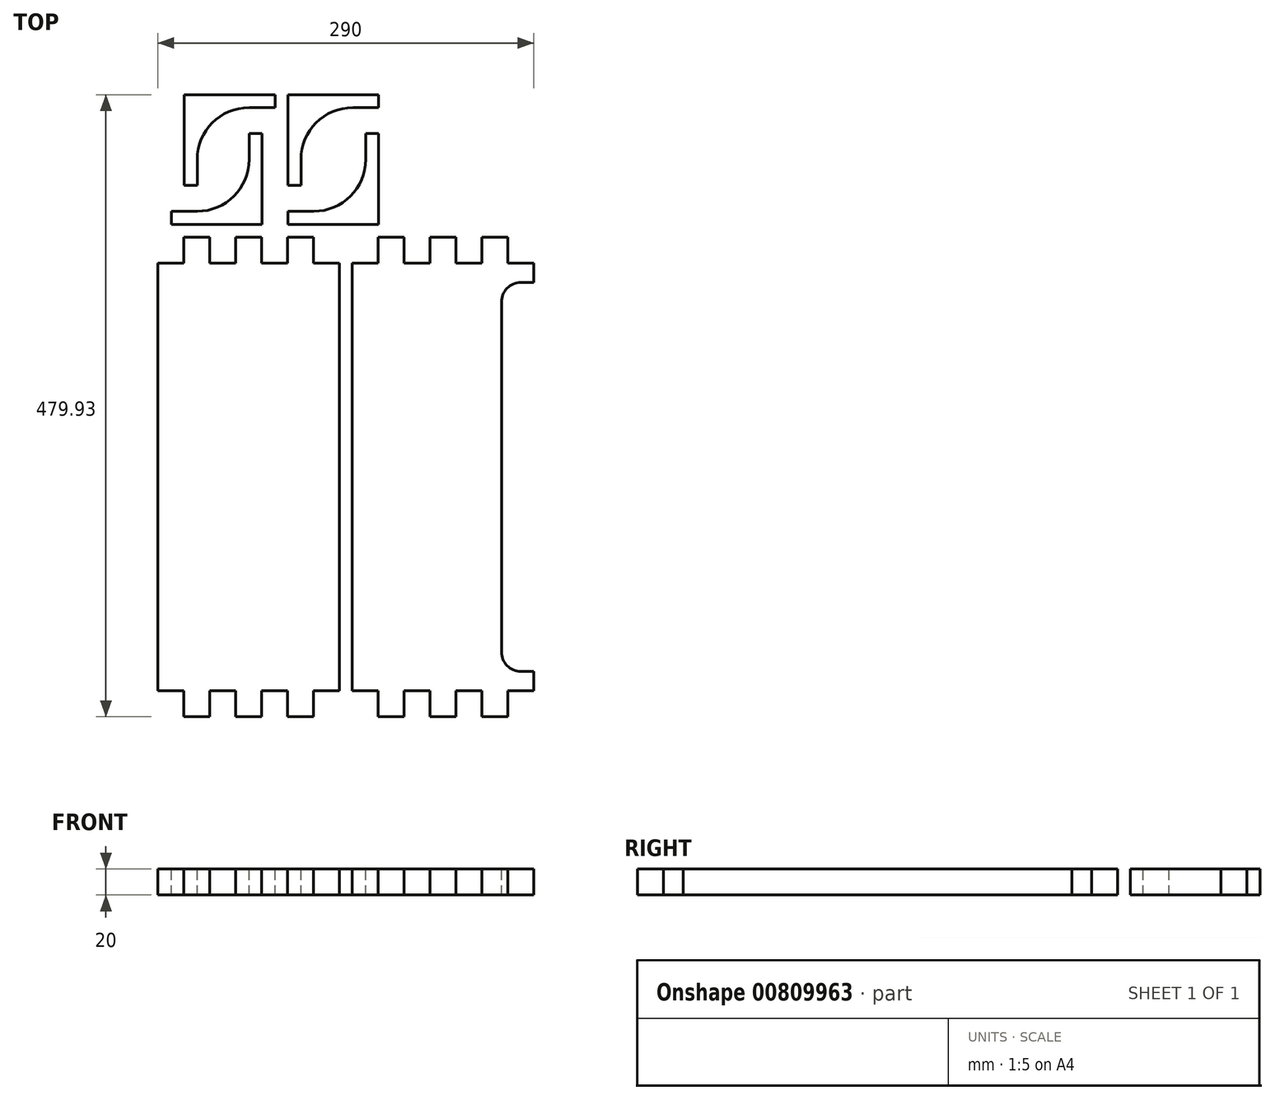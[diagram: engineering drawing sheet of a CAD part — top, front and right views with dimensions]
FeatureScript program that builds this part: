
annotation { "Feature Type Name" : "Feature", "Feature Type Description" : "" }
export const myFeature = defineFeature(function(context is Context, id is Id, definition is map)
    precondition{}
    {
        {
            var Q0;
            Q0=qCreatedBy(makeId("Top.planeOp"),FACE);
            var sketch = newSketch(context, id + "F0", { "sketchPlane" : qUnion([Q0])});
            skLineSegment(sketch, "E0", {"start": v(-70, 25) * mm, "end": v(-50, 25) * mm});
            skLineSegment(sketch, "E1", {"start": v(-50, 25) * mm, "end": v(-50, 5) * mm});
            skLineSegment(sketch, "E2", {"start": v(-50, 5) * mm, "end": v(-30, 5) * mm});
            skLineSegment(sketch, "E3", {"start": v(-30, 5) * mm, "end": v(-30, 25) * mm});
            skLineSegment(sketch, "E4", {"start": v(-30, 25) * mm, "end": v(-10, 25) * mm});
            skLineSegment(sketch, "E5", {"start": v(-10, 25) * mm, "end": v(-10, 5) * mm});
            skLineSegment(sketch, "E6", {"start": v(-10, 5) * mm, "end": v(10, 5) * mm});
            skLineSegment(sketch, "E7", {"start": v(10, 5) * mm, "end": v(10, 25) * mm});
            skLineSegment(sketch, "E8", {"start": v(10, 25) * mm, "end": v(30, 25) * mm});
            skLineSegment(sketch, "E9", {"start": v(30, 25) * mm, "end": v(30, 5) * mm});
            skLineSegment(sketch, "E10", {"start": v(30, 5) * mm, "end": v(50, 5) * mm});
            skLineSegment(sketch, "E11", {"start": v(50, 5) * mm, "end": v(50, 25) * mm});
            skLineSegment(sketch, "E12", {"start": v(50, 25) * mm, "end": v(70, 25) * mm});
            skLineSegment(sketch, "E13", {"start": v(-70, 25) * mm, "end": v(-70, 190) * mm});
            skLineSegment(sketch, "E14", {"start": v(70, 190) * mm, "end": v(70, 25) * mm});
            skLineSegment(sketch, "E15.MirrorCS", {"start": v(-10, 355) * mm, "end": v(-10, 375) * mm});
            skLineSegment(sketch, "E16.MirrorCS", {"start": v(-50, 355) * mm, "end": v(-50, 375) * mm});
            skLineSegment(sketch, "E17.MirrorCS", {"start": v(10, 375) * mm, "end": v(10, 355) * mm});
            skLineSegment(sketch, "E18.MirrorCS", {"start": v(-30, 355) * mm, "end": v(-10, 355) * mm});
            skLineSegment(sketch, "E19.MirrorCS", {"start": v(50, 355) * mm, "end": v(70, 355) * mm});
            skLineSegment(sketch, "E20.MirrorCS", {"start": v(-50, 375) * mm, "end": v(-30, 375) * mm});
            skLineSegment(sketch, "E21.MirrorCS", {"start": v(30, 375) * mm, "end": v(50, 375) * mm});
            skLineSegment(sketch, "E22.MirrorCS", {"start": v(30, 355) * mm, "end": v(30, 375) * mm});
            skLineSegment(sketch, "E23.MirrorCS", {"start": v(10, 355) * mm, "end": v(30, 355) * mm});
            skLineSegment(sketch, "E24.MirrorCS", {"start": v(-70, 355) * mm, "end": v(-50, 355) * mm});
            skLineSegment(sketch, "E25.MirrorCS", {"start": v(70, 190) * mm, "end": v(70, 355) * mm});
            skLineSegment(sketch, "E26.MirrorCS", {"start": v(-10, 375) * mm, "end": v(10, 375) * mm});
            skLineSegment(sketch, "E27.MirrorCS", {"start": v(-70, 355) * mm, "end": v(-70, 190) * mm});
            skLineSegment(sketch, "E28.MirrorCS", {"start": v(50, 375) * mm, "end": v(50, 355) * mm});
            skLineSegment(sketch, "E29.MirrorCS", {"start": v(-30, 375) * mm, "end": v(-30, 355) * mm});
            skLineSegment(sketch, "E30.MirrorCS", {"start": v(220, 25) * mm, "end": v(200, 25) * mm});
            skLineSegment(sketch, "E31.MirrorCS", {"start": v(180, 375) * mm, "end": v(180, 355) * mm});
            skLineSegment(sketch, "E32.MirrorCS", {"start": v(100, 375) * mm, "end": v(100, 355) * mm});
            skLineSegment(sketch, "E33.MirrorCS", {"start": v(160, 375) * mm, "end": v(140, 375) * mm});
            skLineSegment(sketch, "E34.MirrorCS", {"start": v(100, 25) * mm, "end": v(80, 25) * mm});
            skLineSegment(sketch, "E35.MirrorCS", {"start": v(140, 375) * mm, "end": v(140, 355) * mm});
            skLineSegment(sketch, "E36.MirrorCS", {"start": v(180, 25) * mm, "end": v(160, 25) * mm});
            skLineSegment(sketch, "E37.MirrorCS", {"start": v(100, 5) * mm, "end": v(100, 25) * mm});
            skLineSegment(sketch, "E38.MirrorCS", {"start": v(200, 355) * mm, "end": v(200, 375) * mm});
            skLineSegment(sketch, "E39.MirrorCS", {"start": v(180, 5) * mm, "end": v(180, 25) * mm});
            skLineSegment(sketch, "E40.MirrorCS", {"start": v(120, 5) * mm, "end": v(100, 5) * mm});
            skLineSegment(sketch, "E41.MirrorCS", {"start": v(140, 355) * mm, "end": v(120, 355) * mm});
            skLineSegment(sketch, "E42.MirrorCS", {"start": v(160, 355) * mm, "end": v(160, 375) * mm});
            skLineSegment(sketch, "E43.MirrorCS", {"start": v(200, 5) * mm, "end": v(180, 5) * mm});
            skLineSegment(sketch, "E44.MirrorCS", {"start": v(120, 25) * mm, "end": v(120, 5) * mm});
            skLineSegment(sketch, "E45.MirrorCS", {"start": v(120, 355) * mm, "end": v(120, 375) * mm});
            skLineSegment(sketch, "E46.MirrorCS", {"start": v(200, 25) * mm, "end": v(200, 5) * mm});
            skLineSegment(sketch, "E47.MirrorCS", {"start": v(140, 25) * mm, "end": v(120, 25) * mm});
            skLineSegment(sketch, "E48.MirrorCS", {"start": v(120, 375) * mm, "end": v(100, 375) * mm});
            skLineSegment(sketch, "E49.MirrorCS", {"start": v(200, 375) * mm, "end": v(180, 375) * mm});
            skLineSegment(sketch, "E50.MirrorCS", {"start": v(140, 5) * mm, "end": v(140, 25) * mm});
            skLineSegment(sketch, "E51.MirrorCS", {"start": v(100, 355) * mm, "end": v(80, 355) * mm});
            skLineSegment(sketch, "E52.MirrorCS", {"start": v(160, 5) * mm, "end": v(140, 5) * mm});
            skLineSegment(sketch, "E53.MirrorCS", {"start": v(180, 355) * mm, "end": v(160, 355) * mm});
            skLineSegment(sketch, "E54.MirrorCS", {"start": v(160, 25) * mm, "end": v(160, 5) * mm});
            skLineSegment(sketch, "E55.MirrorCS", {"start": v(220, 355) * mm, "end": v(200, 355) * mm});
            skLineSegment(sketch, "E56", {"start": v(220, 355) * mm, "end": v(220, 340) * mm});
            skLineSegment(sketch, "E57", {"start": v(220, 25) * mm, "end": v(220, 40) * mm});
            skLineSegment(sketch, "E58", {"start": v(80, 355) * mm, "end": v(80, 25) * mm});
            skArc(sketch, "E59", {"start": v(220, 340) * mm, "mid": v(202.32, 332.68) * mm, "end": v(195, 315) * mm});
            skArc(sketch, "E60.MirrorCS", {"start": v(220, 40) * mm, "mid": v(202.32, 47.32) * mm, "end": v(195, 65) * mm});
            skLineSegment(sketch, "E61", {"start": v(195, 315) * mm, "end": v(195, 65) * mm});
            skLineSegment(sketch, "E62", {"start": v(-70, 385) * mm, "end": v(-70, 455) * mm});
            skLineSegment(sketch, "E63", {"start": v(-70, 455) * mm, "end": v(0, 455) * mm});
            skLineSegment(sketch, "E64", {"start": v(-70, 385) * mm, "end": v(-55, 385) * mm});
            skLineSegment(sketch, "E65", {"start": v(0, 455) * mm, "end": v(0, 440) * mm});
            skLineSegment(sketch, "E66", {"start": v(-55, 385) * mm, "end": v(-55, 400) * mm});
            skLineSegment(sketch, "E67", {"start": v(0, 440) * mm, "end": v(-15, 440) * mm});
            skArc(sketch, "E68", {"start": v(-15, 440) * mm, "mid": v(-43.28, 428.28) * mm, "end": v(-55, 400) * mm});
            skLineSegment(sketch, "E69", {"start": v(10, 455) * mm, "end": v(25, 455) * mm});
            skLineSegment(sketch, "E70", {"start": v(25, 455) * mm, "end": v(25, 385) * mm});
            skLineSegment(sketch, "E71", {"start": v(25, 385) * mm, "end": v(-45, 385) * mm});
            skLineSegment(sketch, "E72", {"start": v(-45, 385) * mm, "end": v(-45, 400) * mm});
            skLineSegment(sketch, "E73", {"start": v(-45, 400) * mm, "end": v(-30, 400) * mm});
            skLineSegment(sketch, "E74", {"start": v(10, 455) * mm, "end": v(10, 440) * mm});
            skArc(sketch, "E75", {"start": v(-30, 400) * mm, "mid": v(-1.72, 411.72) * mm, "end": v(10, 440) * mm});
            skLineSegment(sketch, "E76.MirrorCS", {"start": v(90, 455) * mm, "end": v(90, 440) * mm});
            skLineSegment(sketch, "E77.MirrorCS", {"start": v(145, 385) * mm, "end": v(145, 400) * mm});
            skLineSegment(sketch, "E78.MirrorCS", {"start": v(170, 385) * mm, "end": v(170, 455) * mm});
            skArc(sketch, "E79.MirrorCS", {"start": v(115, 440) * mm, "mid": v(143.28, 428.28) * mm, "end": v(155, 400) * mm});
            skLineSegment(sketch, "E80.MirrorCS", {"start": v(100, 440) * mm, "end": v(115, 440) * mm});
            skLineSegment(sketch, "E81.MirrorCS", {"start": v(155, 385) * mm, "end": v(155, 400) * mm});
            skLineSegment(sketch, "E82.MirrorCS", {"start": v(145, 400) * mm, "end": v(130, 400) * mm});
            skLineSegment(sketch, "E83.MirrorCS", {"start": v(170, 385) * mm, "end": v(155, 385) * mm});
            skLineSegment(sketch, "E84.MirrorCS", {"start": v(75, 385) * mm, "end": v(145, 385) * mm});
            skLineSegment(sketch, "E85.MirrorCS", {"start": v(75, 455) * mm, "end": v(75, 385) * mm});
            skLineSegment(sketch, "E86.MirrorCS", {"start": v(170, 455) * mm, "end": v(100, 455) * mm});
            skArc(sketch, "E87.MirrorCS", {"start": v(130, 400) * mm, "mid": v(101.72, 411.72) * mm, "end": v(90, 440) * mm});
            skLineSegment(sketch, "E88.MirrorCS", {"start": v(90, 455) * mm, "end": v(75, 455) * mm});
            skLineSegment(sketch, "E89.MirrorCS", {"start": v(100, 455) * mm, "end": v(100, 440) * mm});
            skLineSegment(sketch, "E90", {"start": v(220, -250) * mm, "end": v(220, -473) * mm});
            skLineSegment(sketch, "E91", {"start": v(80, -250) * mm, "end": v(80, -473) * mm});
            skLineSegment(sketch, "E92", {"start": v(220, -473) * mm, "end": v(220, -495) * mm});
            skLineSegment(sketch, "E93", {"start": v(80, -473) * mm, "end": v(80, -495) * mm});
            skLineSegment(sketch, "E94", {"start": v(80, -495) * mm, "end": v(99.5, -495) * mm});
            skLineSegment(sketch, "E95", {"start": v(99.5, -495) * mm, "end": v(99.5, -473) * mm});
            skLineSegment(sketch, "E96", {"start": v(99.5, -473) * mm, "end": v(120.5, -473) * mm});
            skLineSegment(sketch, "E97", {"start": v(120.5, -473) * mm, "end": v(120.5, -495) * mm});
            skLineSegment(sketch, "E98", {"start": v(120.5, -495) * mm, "end": v(139.5, -495) * mm});
            skLineSegment(sketch, "E99", {"start": v(139.5, -495) * mm, "end": v(139.5, -473) * mm});
            skLineSegment(sketch, "E100", {"start": v(139.5, -473) * mm, "end": v(160.5, -473) * mm});
            skLineSegment(sketch, "E101", {"start": v(160.5, -473) * mm, "end": v(160.5, -495) * mm});
            skLineSegment(sketch, "E102", {"start": v(160.5, -495) * mm, "end": v(179.5, -495) * mm});
            skLineSegment(sketch, "E103", {"start": v(179.5, -495) * mm, "end": v(179.5, -473) * mm});
            skLineSegment(sketch, "E104", {"start": v(179.5, -473) * mm, "end": v(200.5, -473) * mm});
            skLineSegment(sketch, "E105", {"start": v(200.5, -473) * mm, "end": v(200.5, -495) * mm});
            skLineSegment(sketch, "E106", {"start": v(200.5, -495) * mm, "end": v(220, -495) * mm});
            skLineSegment(sketch, "E107.MirrorCS", {"start": v(99.5, -27) * mm, "end": v(120.5, -27) * mm});
            skLineSegment(sketch, "E108.MirrorCS", {"start": v(200.5, -5) * mm, "end": v(220, -5) * mm});
            skLineSegment(sketch, "E109.MirrorCS", {"start": v(120.5, -5) * mm, "end": v(139.5, -5) * mm});
            skLineSegment(sketch, "E110.MirrorCS", {"start": v(139.5, -27) * mm, "end": v(160.5, -27) * mm});
            skLineSegment(sketch, "E111.MirrorCS", {"start": v(179.5, -5) * mm, "end": v(179.5, -27) * mm});
            skLineSegment(sketch, "E112.MirrorCS", {"start": v(220, -27) * mm, "end": v(220, -5) * mm});
            skLineSegment(sketch, "E113.MirrorCS", {"start": v(120.5, -27) * mm, "end": v(120.5, -5) * mm});
            skLineSegment(sketch, "E114.MirrorCS", {"start": v(80, -5) * mm, "end": v(99.5, -5) * mm});
            skLineSegment(sketch, "E115.MirrorCS", {"start": v(179.5, -27) * mm, "end": v(200.5, -27) * mm});
            skLineSegment(sketch, "E116.MirrorCS", {"start": v(139.5, -5) * mm, "end": v(139.5, -27) * mm});
            skLineSegment(sketch, "E117.MirrorCS", {"start": v(200.5, -27) * mm, "end": v(200.5, -5) * mm});
            skLineSegment(sketch, "E118.MirrorCS", {"start": v(99.5, -5) * mm, "end": v(99.5, -27) * mm});
            skLineSegment(sketch, "E119.MirrorCS", {"start": v(160.5, -5) * mm, "end": v(179.5, -5) * mm});
            skLineSegment(sketch, "E120.MirrorCS", {"start": v(160.5, -27) * mm, "end": v(160.5, -5) * mm});
            skLineSegment(sketch, "E121.MirrorCS", {"start": v(80, -27) * mm, "end": v(80, -5) * mm});
            skLineSegment(sketch, "E122.MirrorCS", {"start": v(80, -250) * mm, "end": v(80, -27) * mm});
            skLineSegment(sketch, "E123.MirrorCS", {"start": v(220, -250) * mm, "end": v(220, -27) * mm});
            skLineSegment(sketch, "E124.MirrorCS", {"start": v(29.5, -5) * mm, "end": v(10.5, -5) * mm});
            skLineSegment(sketch, "E125.MirrorCS", {"start": v(-70, -27) * mm, "end": v(-70, -5) * mm});
            skLineSegment(sketch, "E126.MirrorCS", {"start": v(10.5, -27) * mm, "end": v(-10.5, -27) * mm});
            skLineSegment(sketch, "E127.MirrorCS", {"start": v(10.5, -5) * mm, "end": v(10.5, -27) * mm});
            skLineSegment(sketch, "E128.MirrorCS", {"start": v(-50.5, -473) * mm, "end": v(-50.5, -495) * mm});
            skLineSegment(sketch, "E129.MirrorCS", {"start": v(-50.5, -495) * mm, "end": v(-70, -495) * mm});
            skLineSegment(sketch, "E130.MirrorCS", {"start": v(-29.5, -473) * mm, "end": v(-50.5, -473) * mm});
            skLineSegment(sketch, "E131.MirrorCS", {"start": v(50.5, -5) * mm, "end": v(50.5, -27) * mm});
            skLineSegment(sketch, "E132.MirrorCS", {"start": v(50.5, -495) * mm, "end": v(50.5, -473) * mm});
            skLineSegment(sketch, "E133.MirrorCS", {"start": v(-70, -473) * mm, "end": v(-70, -495) * mm});
            skLineSegment(sketch, "E134.MirrorCS", {"start": v(-10.5, -27) * mm, "end": v(-10.5, -5) * mm});
            skLineSegment(sketch, "E135.MirrorCS", {"start": v(-29.5, -495) * mm, "end": v(-29.5, -473) * mm});
            skLineSegment(sketch, "E136.MirrorCS", {"start": v(-10.5, -5) * mm, "end": v(-29.5, -5) * mm});
            skLineSegment(sketch, "E137.MirrorCS", {"start": v(29.5, -27) * mm, "end": v(29.5, -5) * mm});
            skLineSegment(sketch, "E138.MirrorCS", {"start": v(-29.5, -27) * mm, "end": v(-50.5, -27) * mm});
            skLineSegment(sketch, "E139.MirrorCS", {"start": v(-50.5, -5) * mm, "end": v(-70, -5) * mm});
            skLineSegment(sketch, "E140.MirrorCS", {"start": v(10.5, -495) * mm, "end": v(10.5, -473) * mm});
            skLineSegment(sketch, "E141.MirrorCS", {"start": v(-50.5, -27) * mm, "end": v(-50.5, -5) * mm});
            skLineSegment(sketch, "E142.MirrorCS", {"start": v(50.5, -473) * mm, "end": v(29.5, -473) * mm});
            skLineSegment(sketch, "E143.MirrorCS", {"start": v(50.5, -27) * mm, "end": v(29.5, -27) * mm});
            skLineSegment(sketch, "E144.MirrorCS", {"start": v(29.5, -473) * mm, "end": v(29.5, -495) * mm});
            skLineSegment(sketch, "E145.MirrorCS", {"start": v(29.5, -495) * mm, "end": v(10.5, -495) * mm});
            skLineSegment(sketch, "E146.MirrorCS", {"start": v(10.5, -473) * mm, "end": v(-10.5, -473) * mm});
            skLineSegment(sketch, "E147.MirrorCS", {"start": v(-10.5, -473) * mm, "end": v(-10.5, -495) * mm});
            skLineSegment(sketch, "E148.MirrorCS", {"start": v(-29.5, -5) * mm, "end": v(-29.5, -27) * mm});
            skLineSegment(sketch, "E149.MirrorCS", {"start": v(-10.5, -495) * mm, "end": v(-29.5, -495) * mm});
            skLineSegment(sketch, "E150.MirrorCS", {"start": v(-70, -250) * mm, "end": v(-70, -473) * mm});
            skLineSegment(sketch, "E151.MirrorCS", {"start": v(-70, -250) * mm, "end": v(-70, -27) * mm});
            skLineSegment(sketch, "E152.MirrorCS", {"start": v(70, -495) * mm, "end": v(50.5, -495) * mm});
            skLineSegment(sketch, "E153.MirrorCS", {"start": v(70, -473) * mm, "end": v(70, -495) * mm});
            skLineSegment(sketch, "E154.MirrorCS", {"start": v(70, -5) * mm, "end": v(50.5, -5) * mm});
            skLineSegment(sketch, "E155.MirrorCS", {"start": v(70, -250) * mm, "end": v(70, -473) * mm});
            skLineSegment(sketch, "E156.MirrorCS", {"start": v(70, -27) * mm, "end": v(70, -5) * mm});
            skLineSegment(sketch, "E157.MirrorCS", {"start": v(70, -250) * mm, "end": v(70, -27) * mm});
            skSolve(sketch);
        }
        {
            var Q0;
            Q0=makeQuery(id+"F0.imprint","IMPRINT",FACE,{"disambiguationData":[TD([[makeQuery(id+"F0.imprint","IMPRINT",EDGE,{"derivedFrom":sQuery(id+"F0.wireOp",EDGE,"A6pHakjd-yKQe-nm1K-0tNp-iDkoEFUulaTX")}),1.0]])]});
            var Q1;
            Q1=makeQuery(id+"F0.imprint","IMPRINT",FACE,{"disambiguationData":[TD([[makeQuery(id+"F0.imprint","IMPRINT",EDGE,{"derivedFrom":sQuery(id+"F0.wireOp",EDGE,"E0")}),1.0]])]});
            var Q2;
            Q2=makeQuery(id+"F0.imprint","IMPRINT",FACE,{"disambiguationData":[TD([[makeQuery(id+"F0.imprint","IMPRINT",EDGE,{"derivedFrom":sQuery(id+"F0.wireOp",EDGE,"uPfnNGFR-UPue-NNoT-3j9v-DdDS5wIcHmke")}),-1.0]])]});
            extrude(context, id + "F1", {"entities" : qUnion([Q0, Q1, Q2]), "depth" : 20 * mm, "offsetDistance" : 25 * mm});
        }
        {
            var Q0;
            Q0=makeQuery(id+"F1.opExtrude","SWEPT_BODY",BODY,{"disambiguationData":[OSD([sQuery(id+"F0.wireOp",EDGE,"uPfnNGFR-UPue-NNoT-3j9v-DdDS5wIcHmke"),sQuery(id+"F0.wireOp",EDGE,"DPA92Joj-OVFD-25TD-bBxH-DW3LVlzY5RxM"),sQuery(id+"F0.wireOp",EDGE,"BTlWhUmO-CDWX-wDiT-Bkhg-RYt8r4K2ftCZ"),sQuery(id+"F0.wireOp",EDGE,"SlLB2Cct-1KW2-f3E8-lR21-xb6hDkdcUdHg"),sQuery(id+"F0.wireOp",EDGE,"x8IDPUu9-QwLP-DRZa-uBUx-mJ2Aen0MBBdt"),sQuery(id+"F0.wireOp",EDGE,"28Rz5wef-z6fz-jzrf-E3N7-LX2DQl9pvpmI"),sQuery(id+"F0.wireOp",EDGE,"czBVLXYd-JF6C-C0VU-R4m2-P8hD6lkvrImN"),sQuery(id+"F0.wireOp",EDGE,"BpHN6O5N-Cw8K-Y1Tr-aEVE-qrIAUK4c1Ka1"),sQuery(id+"F0.wireOp",EDGE,"nlCxKGD2-PE6A-MzsV-HHuT-BGimRYupd8an"),sQuery(id+"F0.wireOp",EDGE,"QyDT4xOd-rL5u-PsyF-biV8-MZHZZoDWxkvl"),sQuery(id+"F0.wireOp",EDGE,"Y3oLtoGm-tCXv-opbv-pqRj-BIGR6ucBVE6h"),sQuery(id+"F0.wireOp",EDGE,"a2csQBM8-Fb0a-SqGs-Ai8H-UW4IMOXVNTeV"),sQuery(id+"F0.wireOp",EDGE,"wntqsrpZ-YtHA-Z1fa-mWbk-3GCJ4Mme8jKI"),sQuery(id+"F0.wireOp",EDGE,"tabSUY3d-DvCt-65x1-RBqV-4sqpVxePUgf1"),sQuery(id+"F0.wireOp",EDGE,"DaWjthnF-SmW0-mPZV-YCG4-CX39uBdR34z2"),sQuery(id+"F0.wireOp",EDGE,"dWbqFZH2-eosh-hLEF-gVrW-tfW1BFaMIpi9"),sQuery(id+"F0.wireOp",EDGE,"5titH3qh-b5Nh-dq2S-g9hr-elYdEYmxVO15"),sQuery(id+"F0.wireOp",EDGE,"e453777b-2879-4b20-a696-1db7350926440.MirrorCS"),sQuery(id+"F0.wireOp",EDGE,"e453777b-2879-4b20-a696-1db7350926441.MirrorCS"),sQuery(id+"F0.wireOp",EDGE,"e453777b-2879-4b20-a696-1db7350926442.MirrorCS"),sQuery(id+"F0.wireOp",EDGE,"e453777b-2879-4b20-a696-1db7350926443.MirrorCS"),sQuery(id+"F0.wireOp",EDGE,"e453777b-2879-4b20-a696-1db7350926444.MirrorCS"),sQuery(id+"F0.wireOp",EDGE,"e453777b-2879-4b20-a696-1db7350926445.MirrorCS"),sQuery(id+"F0.wireOp",EDGE,"e453777b-2879-4b20-a696-1db7350926446.MirrorCS"),sQuery(id+"F0.wireOp",EDGE,"e453777b-2879-4b20-a696-1db7350926447.MirrorCS"),sQuery(id+"F0.wireOp",EDGE,"e453777b-2879-4b20-a696-1db7350926448.MirrorCS"),sQuery(id+"F0.wireOp",EDGE,"e453777b-2879-4b20-a696-1db7350926449.MirrorCS"),sQuery(id+"F0.wireOp",EDGE,"e453777b-2879-4b20-a696-1db73509264410.MirrorCS"),sQuery(id+"F0.wireOp",EDGE,"e453777b-2879-4b20-a696-1db73509264411.MirrorCS"),sQuery(id+"F0.wireOp",EDGE,"e453777b-2879-4b20-a696-1db73509264412.MirrorCS"),sQuery(id+"F0.wireOp",EDGE,"e453777b-2879-4b20-a696-1db73509264413.MirrorCS"),sQuery(id+"F0.wireOp",EDGE,"e453777b-2879-4b20-a696-1db73509264414.MirrorCS"),sQuery(id+"F0.wireOp",EDGE,"e453777b-2879-4b20-a696-1db73509264415.MirrorCS"),sQuery(id+"F0.wireOp",EDGE,"e453777b-2879-4b20-a696-1db73509264416.MirrorCS")])]});
            var Q1;
            Q1=makeQuery(id+"F1.opExtrude","SWEPT_BODY",BODY,{"disambiguationData":[OSD([sQuery(id+"F0.wireOp",EDGE,"E0"),sQuery(id+"F0.wireOp",EDGE,"E1"),sQuery(id+"F0.wireOp",EDGE,"E2"),sQuery(id+"F0.wireOp",EDGE,"E3"),sQuery(id+"F0.wireOp",EDGE,"E4"),sQuery(id+"F0.wireOp",EDGE,"E5"),sQuery(id+"F0.wireOp",EDGE,"E6"),sQuery(id+"F0.wireOp",EDGE,"E7"),sQuery(id+"F0.wireOp",EDGE,"E8"),sQuery(id+"F0.wireOp",EDGE,"E9"),sQuery(id+"F0.wireOp",EDGE,"E10"),sQuery(id+"F0.wireOp",EDGE,"E11"),sQuery(id+"F0.wireOp",EDGE,"E12"),sQuery(id+"F0.wireOp",EDGE,"E13"),sQuery(id+"F0.wireOp",EDGE,"E14"),sQuery(id+"F0.wireOp",EDGE,"E15.MirrorCS"),sQuery(id+"F0.wireOp",EDGE,"E16.MirrorCS"),sQuery(id+"F0.wireOp",EDGE,"E17.MirrorCS"),sQuery(id+"F0.wireOp",EDGE,"E18.MirrorCS"),sQuery(id+"F0.wireOp",EDGE,"E19.MirrorCS"),sQuery(id+"F0.wireOp",EDGE,"E20.MirrorCS"),sQuery(id+"F0.wireOp",EDGE,"E21.MirrorCS"),sQuery(id+"F0.wireOp",EDGE,"E22.MirrorCS"),sQuery(id+"F0.wireOp",EDGE,"E23.MirrorCS"),sQuery(id+"F0.wireOp",EDGE,"E24.MirrorCS"),sQuery(id+"F0.wireOp",EDGE,"E25.MirrorCS"),sQuery(id+"F0.wireOp",EDGE,"E26.MirrorCS"),sQuery(id+"F0.wireOp",EDGE,"E27.MirrorCS"),sQuery(id+"F0.wireOp",EDGE,"E28.MirrorCS"),sQuery(id+"F0.wireOp",EDGE,"E29.MirrorCS")])]});
            transform(context, id + "F2", {"entities" : qUnion([Q0, Q1]), "transformType" : TransformType.COPY});
        }
        {
            var Q0;
            Q0=makeQuery(id+"F2.opPattern","COPY",BODY,{"derivedFrom":makeQuery(id+"F1.opExtrude","SWEPT_BODY",BODY,{"disambiguationData":[OSD([sQuery(id+"F0.wireOp",EDGE,"uPfnNGFR-UPue-NNoT-3j9v-DdDS5wIcHmke"),sQuery(id+"F0.wireOp",EDGE,"DPA92Joj-OVFD-25TD-bBxH-DW3LVlzY5RxM"),sQuery(id+"F0.wireOp",EDGE,"BTlWhUmO-CDWX-wDiT-Bkhg-RYt8r4K2ftCZ"),sQuery(id+"F0.wireOp",EDGE,"SlLB2Cct-1KW2-f3E8-lR21-xb6hDkdcUdHg"),sQuery(id+"F0.wireOp",EDGE,"x8IDPUu9-QwLP-DRZa-uBUx-mJ2Aen0MBBdt"),sQuery(id+"F0.wireOp",EDGE,"28Rz5wef-z6fz-jzrf-E3N7-LX2DQl9pvpmI"),sQuery(id+"F0.wireOp",EDGE,"czBVLXYd-JF6C-C0VU-R4m2-P8hD6lkvrImN"),sQuery(id+"F0.wireOp",EDGE,"BpHN6O5N-Cw8K-Y1Tr-aEVE-qrIAUK4c1Ka1"),sQuery(id+"F0.wireOp",EDGE,"nlCxKGD2-PE6A-MzsV-HHuT-BGimRYupd8an"),sQuery(id+"F0.wireOp",EDGE,"QyDT4xOd-rL5u-PsyF-biV8-MZHZZoDWxkvl"),sQuery(id+"F0.wireOp",EDGE,"Y3oLtoGm-tCXv-opbv-pqRj-BIGR6ucBVE6h"),sQuery(id+"F0.wireOp",EDGE,"a2csQBM8-Fb0a-SqGs-Ai8H-UW4IMOXVNTeV"),sQuery(id+"F0.wireOp",EDGE,"wntqsrpZ-YtHA-Z1fa-mWbk-3GCJ4Mme8jKI"),sQuery(id+"F0.wireOp",EDGE,"tabSUY3d-DvCt-65x1-RBqV-4sqpVxePUgf1"),sQuery(id+"F0.wireOp",EDGE,"DaWjthnF-SmW0-mPZV-YCG4-CX39uBdR34z2"),sQuery(id+"F0.wireOp",EDGE,"dWbqFZH2-eosh-hLEF-gVrW-tfW1BFaMIpi9"),sQuery(id+"F0.wireOp",EDGE,"5titH3qh-b5Nh-dq2S-g9hr-elYdEYmxVO15"),sQuery(id+"F0.wireOp",EDGE,"e453777b-2879-4b20-a696-1db7350926440.MirrorCS"),sQuery(id+"F0.wireOp",EDGE,"e453777b-2879-4b20-a696-1db7350926441.MirrorCS"),sQuery(id+"F0.wireOp",EDGE,"e453777b-2879-4b20-a696-1db7350926442.MirrorCS"),sQuery(id+"F0.wireOp",EDGE,"e453777b-2879-4b20-a696-1db7350926443.MirrorCS"),sQuery(id+"F0.wireOp",EDGE,"e453777b-2879-4b20-a696-1db7350926444.MirrorCS"),sQuery(id+"F0.wireOp",EDGE,"e453777b-2879-4b20-a696-1db7350926445.MirrorCS"),sQuery(id+"F0.wireOp",EDGE,"e453777b-2879-4b20-a696-1db7350926446.MirrorCS"),sQuery(id+"F0.wireOp",EDGE,"e453777b-2879-4b20-a696-1db7350926447.MirrorCS"),sQuery(id+"F0.wireOp",EDGE,"e453777b-2879-4b20-a696-1db7350926448.MirrorCS"),sQuery(id+"F0.wireOp",EDGE,"e453777b-2879-4b20-a696-1db7350926449.MirrorCS"),sQuery(id+"F0.wireOp",EDGE,"e453777b-2879-4b20-a696-1db73509264410.MirrorCS"),sQuery(id+"F0.wireOp",EDGE,"e453777b-2879-4b20-a696-1db73509264411.MirrorCS"),sQuery(id+"F0.wireOp",EDGE,"e453777b-2879-4b20-a696-1db73509264412.MirrorCS"),sQuery(id+"F0.wireOp",EDGE,"e453777b-2879-4b20-a696-1db73509264413.MirrorCS"),sQuery(id+"F0.wireOp",EDGE,"e453777b-2879-4b20-a696-1db73509264414.MirrorCS"),sQuery(id+"F0.wireOp",EDGE,"e453777b-2879-4b20-a696-1db73509264415.MirrorCS"),sQuery(id+"F0.wireOp",EDGE,"e453777b-2879-4b20-a696-1db73509264416.MirrorCS")])]}),"instanceName":"1"});
            var Q1;
            Q1=makeQuery(id+"F2.opPattern","COPY",BODY,{"derivedFrom":makeQuery(id+"F1.opExtrude","SWEPT_BODY",BODY,{"disambiguationData":[OSD([sQuery(id+"F0.wireOp",EDGE,"E0"),sQuery(id+"F0.wireOp",EDGE,"E1"),sQuery(id+"F0.wireOp",EDGE,"E2"),sQuery(id+"F0.wireOp",EDGE,"E3"),sQuery(id+"F0.wireOp",EDGE,"E4"),sQuery(id+"F0.wireOp",EDGE,"E5"),sQuery(id+"F0.wireOp",EDGE,"E6"),sQuery(id+"F0.wireOp",EDGE,"E7"),sQuery(id+"F0.wireOp",EDGE,"E8"),sQuery(id+"F0.wireOp",EDGE,"E9"),sQuery(id+"F0.wireOp",EDGE,"E10"),sQuery(id+"F0.wireOp",EDGE,"E11"),sQuery(id+"F0.wireOp",EDGE,"E12"),sQuery(id+"F0.wireOp",EDGE,"E13"),sQuery(id+"F0.wireOp",EDGE,"E14"),sQuery(id+"F0.wireOp",EDGE,"E15.MirrorCS"),sQuery(id+"F0.wireOp",EDGE,"E16.MirrorCS"),sQuery(id+"F0.wireOp",EDGE,"E17.MirrorCS"),sQuery(id+"F0.wireOp",EDGE,"E18.MirrorCS"),sQuery(id+"F0.wireOp",EDGE,"E19.MirrorCS"),sQuery(id+"F0.wireOp",EDGE,"E20.MirrorCS"),sQuery(id+"F0.wireOp",EDGE,"E21.MirrorCS"),sQuery(id+"F0.wireOp",EDGE,"E22.MirrorCS"),sQuery(id+"F0.wireOp",EDGE,"E23.MirrorCS"),sQuery(id+"F0.wireOp",EDGE,"E24.MirrorCS"),sQuery(id+"F0.wireOp",EDGE,"E25.MirrorCS"),sQuery(id+"F0.wireOp",EDGE,"E26.MirrorCS"),sQuery(id+"F0.wireOp",EDGE,"E27.MirrorCS"),sQuery(id+"F0.wireOp",EDGE,"E28.MirrorCS"),sQuery(id+"F0.wireOp",EDGE,"E29.MirrorCS")])]}),"instanceName":"1"});
            transform(context, id + "F3", {"entities" : qUnion([Q0, Q1]), "transformType" : TransformType.TRANSLATION_3D, "dx" : 150 * mm, "dy" : 0 * mm, "dz" : 0 * mm, "makeCopy" : false});
        }
        {
            var Q0;
            Q0=makeQuery(id+"F2.opPattern","COPY",FACE,{"derivedFrom":makeQuery(id+"F1.opExtrude","SWEPT_FACE",FACE,{"disambiguationData":[OSD([sQuery(id+"F0.wireOp",EDGE,"E14"),sQuery(id+"F0.wireOp",EDGE,"E25.MirrorCS")])]}),"instanceName":"1"});
            var sketch = newSketch(context, id + "F4", { "sketchPlane" : qUnion([Q0])});
            skLineSegment(sketch, "E158", {"start": v(40, 0) * mm, "end": v(190, 0) * mm});
            skLineSegment(sketch, "E159", {"start": v(40, 0) * mm, "end": v(40, 20) * mm});
            skLineSegment(sketch, "E160", {"start": v(40, 20) * mm, "end": v(190, 20) * mm});
            skLineSegment(sketch, "E161", {"start": v(190, 20) * mm, "end": v(190, 0) * mm});
            skLineSegment(sketch, "E162.MirrorCS", {"start": v(340, 0) * mm, "end": v(190, 0) * mm});
            skLineSegment(sketch, "E163.MirrorCS", {"start": v(340, 0) * mm, "end": v(340, 20) * mm});
            skLineSegment(sketch, "E164.MirrorCS", {"start": v(340, 20) * mm, "end": v(190, 20) * mm});
            skSolve(sketch);
        }
        {
            var Q0;
            Q0 = qSketchRegion(id + "F4", true);
            extrude(context, id + "F5", {"entities" : qUnion([Q0]), "operationType" : NewBodyOperationType.REMOVE, "oppositeDirection" : true, "depth" : 25 * mm, "offsetDistance" : 25 * mm});
        }
        {
            var Q0;
            Q0=makeQuery(id+"F5.boolean.opBoolean","COPY",EDGE,{"derivedFrom":makeQuery(id+"F5.opExtrude","CAP_EDGE",EDGE,{"disambiguationData":[OSD([sQuery(id+"F4.wireOp",EDGE,"E159")])],"isStart":false})});
            var Q1;
            Q1=makeQuery(id+"F5.boolean.opBoolean","COPY",EDGE,{"derivedFrom":makeQuery(id+"F5.opExtrude","CAP_EDGE",EDGE,{"disambiguationData":[OSD([sQuery(id+"F4.wireOp",EDGE,"E163.MirrorCS")])],"isStart":false})});
            fillet(context, id + "F6", {"entities" : qUnion([Q0, Q1]), "radius" : 15 * mm, "tangentPropagation" : true, "allowEdgeOverflow" : false});
        }
        {
            var Q0;
            Q0=makeQuery(id+"F2.opPattern","COPY",FACE,{"derivedFrom":makeQuery(id+"F1.opExtrude","CAP_FACE",FACE,{"disambiguationData":[OSD([sQuery(id+"F0.wireOp",EDGE,"E0"),sQuery(id+"F0.wireOp",EDGE,"E1"),sQuery(id+"F0.wireOp",EDGE,"E2"),sQuery(id+"F0.wireOp",EDGE,"E3"),sQuery(id+"F0.wireOp",EDGE,"E4"),sQuery(id+"F0.wireOp",EDGE,"E5"),sQuery(id+"F0.wireOp",EDGE,"E6"),sQuery(id+"F0.wireOp",EDGE,"E7"),sQuery(id+"F0.wireOp",EDGE,"E8"),sQuery(id+"F0.wireOp",EDGE,"E9"),sQuery(id+"F0.wireOp",EDGE,"E10"),sQuery(id+"F0.wireOp",EDGE,"E11"),sQuery(id+"F0.wireOp",EDGE,"E12"),sQuery(id+"F0.wireOp",EDGE,"E13"),sQuery(id+"F0.wireOp",EDGE,"E14"),sQuery(id+"F0.wireOp",EDGE,"E15.MirrorCS"),sQuery(id+"F0.wireOp",EDGE,"E16.MirrorCS"),sQuery(id+"F0.wireOp",EDGE,"E17.MirrorCS"),sQuery(id+"F0.wireOp",EDGE,"E18.MirrorCS"),sQuery(id+"F0.wireOp",EDGE,"E19.MirrorCS"),sQuery(id+"F0.wireOp",EDGE,"E20.MirrorCS"),sQuery(id+"F0.wireOp",EDGE,"E21.MirrorCS"),sQuery(id+"F0.wireOp",EDGE,"E22.MirrorCS"),sQuery(id+"F0.wireOp",EDGE,"E23.MirrorCS"),sQuery(id+"F0.wireOp",EDGE,"E24.MirrorCS"),sQuery(id+"F0.wireOp",EDGE,"E25.MirrorCS"),sQuery(id+"F0.wireOp",EDGE,"E26.MirrorCS"),sQuery(id+"F0.wireOp",EDGE,"E27.MirrorCS"),sQuery(id+"F0.wireOp",EDGE,"E28.MirrorCS"),sQuery(id+"F0.wireOp",EDGE,"E29.MirrorCS")])],"isStart":false}),"instanceName":"1"});
            var sketch = newSketch(context, id + "F7", { "sketchPlane" : qUnion([Q0])});
            skLineSegment(sketch, "E165", {"start": v(-49.66, 414.93) * mm, "end": v(-49.66, 484.93) * mm});
            skLineSegment(sketch, "E166", {"start": v(-49.66, 484.93) * mm, "end": v(20.34, 484.93) * mm});
            skLineSegment(sketch, "E167", {"start": v(-49.66, 414.93) * mm, "end": v(-39.66, 414.93) * mm});
            skLineSegment(sketch, "E168", {"start": v(20.34, 484.93) * mm, "end": v(20.34, 474.93) * mm});
            skLineSegment(sketch, "E169", {"start": v(20.34, 474.93) * mm, "end": v(-39.66, 474.93) * mm});
            skLineSegment(sketch, "E170", {"start": v(-39.66, 474.93) * mm, "end": v(-39.66, 414.93) * mm});
            skSolve(sketch);
        }
        {
            var Q0;
            Q0=makeQuery(id+"F7.imprint","IMPRINT",FACE,{"disambiguationData":[TD([[makeQuery(id+"F7.imprint","IMPRINT",EDGE,{"derivedFrom":sQuery(id+"F7.wireOp",EDGE,"E165")}),-1.0]])]});
            extrude(context, id + "F8", {"entities" : qUnion([Q0]), "oppositeDirection" : true, "depth" : 20 * mm, "offsetDistance" : 25 * mm});
        }
        {
            var Q0;
            Q0=makeQuery(id+"F8.opExtrude","SWEPT_EDGE",EDGE,{"disambiguationData":[OSD([sQuery(id+"F7.wireOp",EDGE,"E169"),sQuery(id+"F7.wireOp",EDGE,"E170")])]});
            fillet(context, id + "F9", {"entities" : qUnion([Q0]), "radius" : 40 * mm, "tangentPropagation" : true, "allowEdgeOverflow" : false});
        }
        {
            var Q0;
            Q0=makeQuery(id+"F8.opExtrude","SWEPT_BODY",BODY,{"disambiguationData":[OSD([sQuery(id+"F7.wireOp",EDGE,"E165"),sQuery(id+"F7.wireOp",EDGE,"E166"),sQuery(id+"F7.wireOp",EDGE,"E167"),sQuery(id+"F7.wireOp",EDGE,"E168"),sQuery(id+"F7.wireOp",EDGE,"E169"),sQuery(id+"F7.wireOp",EDGE,"E170")])]});
            transform(context, id + "F10", {"entities" : qUnion([Q0]), "transformType" : TransformType.TRANSLATION_3D, "dx" : 80 * mm, "dy" : 0 * mm, "dz" : 0 * mm, "makeCopy" : true});
        }
        {
            var Q0;
            Q0=makeQuery(id+"F8.opExtrude","SWEPT_BODY",BODY,{"disambiguationData":[OSD([sQuery(id+"F7.wireOp",EDGE,"E165"),sQuery(id+"F7.wireOp",EDGE,"E166"),sQuery(id+"F7.wireOp",EDGE,"E167"),sQuery(id+"F7.wireOp",EDGE,"E168"),sQuery(id+"F7.wireOp",EDGE,"E169"),sQuery(id+"F7.wireOp",EDGE,"E170")])]});
            var Q1;
            Q1=makeQuery(id+"F8.opExtrude","SWEPT_EDGE",EDGE,{"disambiguationData":[OSD([sQuery(id+"F7.wireOp",EDGE,"E165"),sQuery(id+"F7.wireOp",EDGE,"E166")])]});
            transform(context, id + "F11", {"entities" : qUnion([Q0]), "transformType" : TransformType.ROTATION, "transformAxis" : qUnion([Q1]), "angle" : 180 * degree, "makeCopy" : true});
        }
        {
            var Q0;
            Q0=makeQuery(id+"F11.opPattern","COPY",BODY,{"derivedFrom":makeQuery(id+"F8.opExtrude","SWEPT_BODY",BODY,{"disambiguationData":[OSD([sQuery(id+"F7.wireOp",EDGE,"E165"),sQuery(id+"F7.wireOp",EDGE,"E166"),sQuery(id+"F7.wireOp",EDGE,"E167"),sQuery(id+"F7.wireOp",EDGE,"E168"),sQuery(id+"F7.wireOp",EDGE,"E169"),sQuery(id+"F7.wireOp",EDGE,"E170")])]}),"instanceName":"1"});
            transform(context, id + "F12", {"entities" : qUnion([Q0]), "transformType" : TransformType.TRANSLATION_3D, "dx" : 60 * mm, "dy" : -100 * mm, "dz" : 0 * mm, "makeCopy" : true});
        }
        {
            var Q0;
            Q0=makeQuery(id+"F11.opPattern","COPY",BODY,{"derivedFrom":makeQuery(id+"F8.opExtrude","SWEPT_BODY",BODY,{"disambiguationData":[OSD([sQuery(id+"F7.wireOp",EDGE,"E165"),sQuery(id+"F7.wireOp",EDGE,"E166"),sQuery(id+"F7.wireOp",EDGE,"E167"),sQuery(id+"F7.wireOp",EDGE,"E168"),sQuery(id+"F7.wireOp",EDGE,"E169"),sQuery(id+"F7.wireOp",EDGE,"E170")])]}),"instanceName":"1"});
            transform(context, id + "F13", {"entities" : qUnion([Q0]), "transformType" : TransformType.TRANSLATION_3D, "dx" : 150 * mm, "dy" : -100 * mm, "dz" : 0 * mm, "makeCopy" : false});
        }
    });
